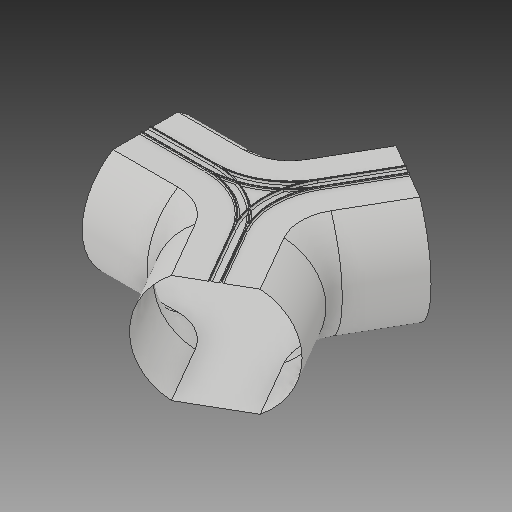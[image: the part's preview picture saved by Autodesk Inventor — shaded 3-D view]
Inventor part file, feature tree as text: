
AUTODESK INVENTOR PART (.ipt)
format: ipt  version: 2017 (Build 210142000, 142)  size: 376,320 bytes
history: native  units: in
note: dims shown in document units (in); Inventor stores cm internally (conversion verified against a paired STEP export)
features: sketch x4, extrude x2, other x2, pattern_circular x2, sweep x1, delete_face x1
ambient origin geometry x8: Origin, YZ Plane, XZ Plane, XY Plane, X Axis, Y Axis, Z Axis, Center Point
bodies: Solid1 (feature_tree)
feature tree (12):
  sketch  "Sketch1"  dims[d10=6.6667in d12=4.0in d13=0.0in d15=2.8217in d16=1.1811in d17=360.0deg]
  extrude  "corridor"  Depth=2.8217in
  other  "found rotaion axis"
  other  "rotaion axis"
  pattern_circular  "other corridors"  Count=3 Angle=360.0deg
  sketch  "Sketch5"  dims[d105=4.0in d106=0.5833in d107=3.8873in d108=3.8873in d109=1.7083in d110=0.0625in d111=0.0625in d112=1.6458in d113=0.25in d114=0.125in d116=0.0884in d117=45.0deg d118=3.3333in d119=0.125in]
  sketch  "Sketch4"  dims[d24=0.0in d25=0.0in d26=1.1811in d27=360.0deg]
  sweep  "curve edjes"
  pattern_circular  "repeat curve edjes"  [2 undecoded]
  extrude  "hole fill in"  [1 undecoded]
  delete_face  "Delete Face1"
  sketch  "Sketch10"  dims[d120=1.0in d121=0.0in]
note: 3 required parameter values undecoded (feature->parameter linkage not recoverable at this tier; creation-order binding heuristic only, values carry confidence <= 0.55)
